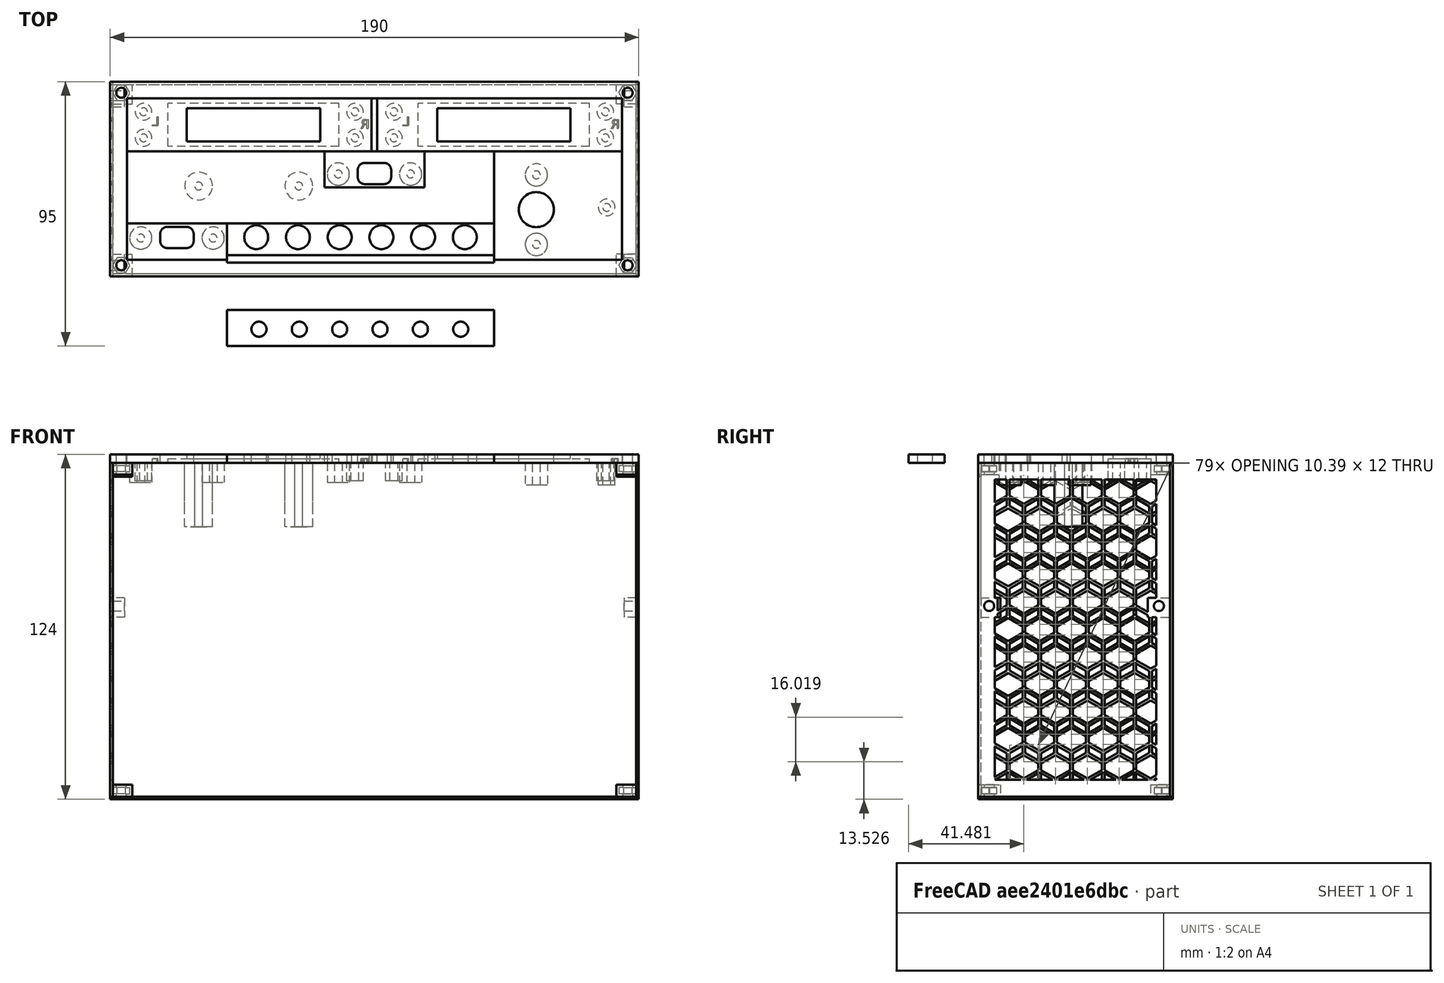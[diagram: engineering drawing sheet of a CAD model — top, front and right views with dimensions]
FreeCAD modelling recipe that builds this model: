
FCSTD DOCUMENT  (FreeCAD 0.18.4R)
Label: radio_led_grande
License: All rights reserved
LicenseURL: http://en.wikipedia.org/wiki/All_rights_reserved
objects: Part::Box×55, Part::Cut×51, Part::MultiFuse×42, Part::Cylinder×30, Part::Feature×20, Part::Prism×8, TechDraw::DrawSVGTemplate×1, TechDraw::DrawViewPart×1, TechDraw::DrawPage×1
note: 206 computed .brp shape members not serialized (recipe doc carries the construction recipe); baked Part::Feature solids carry a one-line shape summary decoded from their .brp

FEATURE [Part::Box] Box  label="Cube"
  AttacherType = Attacher::AttachEngine3D
  Height = 3
  Length = 190
  Width = 70
FEATURE [Part::Box] Box001  label="Cube001"
  AttacherType = Attacher::AttachEngine3D
  Height = 3
  Length = 178
  Placement = pos=(6,6,0) rot=(0,0,1;0rad)
  Width = 58
FEATURE [Part::Cut] Cut  label="marco"
  Base = -> Box
  Placement = pos=(-89,19,-107) rot=(0,0,1;0rad)
  Tool = -> Box001
FEATURE [Part::Box] Box002  label="Cube002"
  AttacherType = Attacher::AttachEngine3D
  Height = 3
  Length = 96
  Placement = pos=(-47,25,3) rot=(0,0,1;0rad)
  Width = 13
FEATURE [Part::Cylinder] Cylinder
  Angle = 360
  AttacherType = Attacher::AttachEngine3D
  Height = 10
  Placement = pos=(-35.5,31,0) rot=(0,0,1;0rad)
  Radius = 2.7
FEATURE [Part::Cylinder] Cylinder001 .. Cylinder005  x5 (patterned run collapsed; names and placements below)
  Angle = 360
  AttacherType = Attacher::AttachEngine3D
  Height = 10
  Radius = 2.7
  placements: 5 in arithmetic series — first pos=(-21,31,0) rot=(0,0,1;0rad), step (14.5,0,0), last pos=(37,31,0) rot=(0,0,1;0rad)
FEATURE [Part::Cut] Cut001001001002003001008002002033001001001001001001001002001001002001045002003017008007003
  Base = -> Box002
  Tool = -> Cylinder005
FEATURE [Part::Cut] Cut001001001002003001008002002033001001001001001001001002001001002001045002003017008007004
  Base = -> Cut001001001002003001008002002033001001001001001001001002001001002001045002003017008007003
  Tool = -> Cylinder004
FEATURE [Part::Cut] Cut001001001002003001008002002033001001001001001001001002001001002001045002003017008007005
  Base = -> Cut001001001002003001008002002033001001001001001001001002001001002001045002003017008007004
  Tool = -> Cylinder003
FEATURE [Part::Cut] Cut001001001002003001008002002033001001001001001001001002001001002001045002003017008007006
  Base = -> Cut001001001002003001008002002033001001001001001001001002001001002001045002003017008007005
  Tool = -> Cylinder002
FEATURE [Part::Cut] Cut001001001002003001008002002033001001001001001001001002001001002001045002003017008007007
  Base = -> Cut001001001002003001008002002033001001001001001001001002001001002001045002003017008007006
  Tool = -> Cylinder001
FEATURE [Part::Cut] Cut001001001002003001008002002033001001001001001001001002001001002001045002003017008007008  label="6leds_6mm_diametro"
  Base = -> Cut001001001002003001008002002033001001001001001001001002001001002001045002003017008007007
  Placement = pos=(0,-31,-110) rot=(0,0,1;0rad)
  Tool = -> Cylinder
FEATURE [Part::Box] Box003  label="Cube003"
  AttacherType = Attacher::AttachEngine3D
  Height = 3
  Length = 71
  Placement = pos=(-83,38,-107) rot=(0,0,1;0rad)
  Width = 26
FEATURE [Part::Box] Box004  label="Cube004"
  AttacherType = Attacher::AttachEngine3D
  Height = 3
  Length = 36
  Placement = pos=(-12,38,-107) rot=(0,0,1;0rad)
  Width = 13
FEATURE [Part::Box] Box005  label="Cube005"
  AttacherType = Attacher::AttachEngine3D
  Height = 3
  Length = 25
  Placement = pos=(24,38,-107) rot=(0,0,1;0rad)
  Width = 26
FEATURE [Part::Box] Box006  label="relleno2"
  AttacherType = Attacher::AttachEngine3D
  Height = 3
  Length = 2
  Placement = pos=(5,64,-107) rot=(0,0,1;0rad)
  Width = 19
FEATURE [Part::Box] Box007  label="Cube007"
  AttacherType = Attacher::AttachEngine3D
  Height = 3
  Length = 46
  Placement = pos=(49,61,-107) rot=(0,0,1;0rad)
  Width = 3
FEATURE [Part::Cylinder] Cylinder006
  Angle = 360
  AttacherType = Attacher::AttachEngine3D
  Height = 10
  Placement = pos=(-85,23,-111) rot=(0,0,1;0rad)
  Radius = 1.8
FEATURE [Part::Cylinder] Cylinder007
  Angle = 360
  AttacherType = Attacher::AttachEngine3D
  Height = 10
  Placement = pos=(-85,85,-113) rot=(0,0,1;0rad)
  Radius = 1.8
FEATURE [Part::Cylinder] Cylinder008
  Angle = 360
  AttacherType = Attacher::AttachEngine3D
  Height = 10
  Placement = pos=(97,23,-111) rot=(0,0,1;0rad)
  Radius = 1.8
FEATURE [Part::Cylinder] Cylinder009
  Angle = 360
  AttacherType = Attacher::AttachEngine3D
  Height = 10
  Placement = pos=(97,85,-111) rot=(0,0,1;0rad)
  Radius = 1.8
FEATURE [Part::Cut] Cut001001001002003001008002002033001001001001001001001002001001002001045002003017008007009
  Base = -> Cut
  Tool = -> Cylinder006
FEATURE [Part::Cut] Cut001001001002003001008002002033001001001001001001001002001001002001045002003017008007010
  Base = -> Cut001001001002003001008002002033001001001001001001001002001001002001045002003017008007009
  Tool = -> Cylinder007
FEATURE [Part::Cut] Cut001001001002003001008002002033001001001001001001001002001001002001045002003017008007011
  Base = -> Cut001001001002003001008002002033001001001001001001001002001001002001045002003017008007010
  Tool = -> Cylinder009
FEATURE [Part::Cut] Cut001001001002003001008002002033001001001001001001001002001001002001045002003017008007012  label="marco_con_agujeros"
  Base = -> Cut001001001002003001008002002033001001001001001001001002001001002001045002003017008007011
  Tool = -> Cylinder008
FEATURE [Part::Box] Box008  label="Cube008"
  AttacherType = Attacher::AttachEngine3D
  Height = 3
  Length = 96
  Placement = pos=(-47,24,-107) rot=(0,0,1;0rad)
  Width = 3
FEATURE [Part::MultiFuse] Fusion007002009027003005008003003014  label="soporte_alto_1"
  Placement = pos=(-164,36,0) rot=(0,0,1;0rad)
FEATURE [Part::MultiFuse] Fusion007002009027003005008003003006005002  label="soporte_alto_2"
  Placement = pos=(-128,36,0) rot=(0,0,1;0rad)
FEATURE [Part::Feature] Cut001001001002003001008002002033001001001001001001001002001001002001045002003017008007002010007002014003004001  label="base_boton_bajo_16x038_selector"
  Placement = pos=(-117,37,0) rot=(0,0,1;0rad)
  shape: bbox 36 x 16 x 10 mm, 26 faces (baked)
FEATURE [Part::Feature] Cut001001001002003001008002002033001001001001001001001002001001002001045002003017008007002010007002014003004002  label="base_boton_bajo_16x039_switch"
  Placement = pos=(-46,60,0) rot=(0,0,1;0rad)
  shape: bbox 36 x 16 x 10 mm, 26 faces (baked)
FEATURE [Part::Feature] Cut001001001002003001008002002033001001001001001001001002001001002001045002003017008007002010007002014003013001  label="base_7seg_full_3mm_88x021_stby"
  Placement = pos=(2,0,0) rot=(0,0,1;0rad)
  shape: bbox 88 x 19 x 9.5 mm, 63 faces (baked)
FEATURE [Part::Feature] Cut001001001002003001008002002033001001001001001001001002001001002001045002003017008007002010007002014003013002  label="base_7seg_full_3mm_88x022_act"
  Placement = pos=(-88,0,0) rot=(0,0,1;0rad)
  shape: bbox 88 x 19 x 9.5 mm, 63 faces (baked)
FEATURE [Part::Feature] Fusion007002009027003005008003003018001  label="base_encoder_doble_46x36_agujero_13"
  Placement = pos=(102.5,-18,0) rot=(0,0,1;0rad)
  shape: bbox 46 x 36 x 11 mm, 19 faces (baked)
FEATURE [Part::Feature] Cut001001001002003001008002002033001001001001001001001002001001002001045002003017008007002010007002014003017001  label="base_led_radius_43_ref"
  Placement = pos=(-26,-22,0) rot=(0,0,1;0rad)
  shape: bbox 10.6 x 10.6 x 3 mm, 7 faces (baked)
FEATURE [Part::Feature] Cut001001001002003001008002002033001001001001001001001002001001002001045002003017008007002010007002014003017002  label="base_led_radius_43_ref001"
  Placement = pos=(-11,-22,0) rot=(0,0,1;0rad)
  shape: bbox 10.6 x 10.6 x 3 mm, 7 faces (baked)
FEATURE [Part::Feature] Cut001001001002003001008002002033001001001001001001001002001001002001045002003017008007002010007002014003017003  label="base_led_radius_43_ref002"
  Placement = pos=(4,-22,0) rot=(0,0,1;0rad)
  shape: bbox 10.6 x 10.6 x 3 mm, 7 faces (baked)
FEATURE [Part::Feature] Cut001001001002003001008002002033001001001001001001001002001001002001045002003017008007002010007002014003017004  label="base_led_radius_43_ref003"
  Placement = pos=(19,-22,0) rot=(0,0,1;0rad)
  shape: bbox 10.6 x 10.6 x 3 mm, 7 faces (baked)
FEATURE [Part::Feature] Cut001001001002003001008002002033001001001001001001001002001001002001045002003017008007002010007002014003017005  label="base_led_radius_43_ref004"
  Placement = pos=(34,-22,0) rot=(0,0,1;0rad)
  shape: bbox 10.6 x 10.6 x 3 mm, 7 faces (baked)
FEATURE [Part::Feature] Cut001001001002003001008002002033001001001001001001001002001001002001045002003017008007002010007002014003017006  label="base_led_radius_43_ref005"
  Placement = pos=(49,-22,0) rot=(0,0,1;0rad)
  shape: bbox 10.6 x 10.6 x 3 mm, 7 faces (baked)
FEATURE [Part::Box] Box009  label="Cube009"
  AttacherType = Attacher::AttachEngine3D
  Height = 3
  Length = 96
  Placement = pos=(-31.2,-6.2,-108) rot=(0,0,1;0rad)
  Width = 13
FEATURE [Part::Box] Box010  label="Cube010"
  AttacherType = Attacher::AttachEngine3D
  Height = 3
  Length = 85
  Placement = pos=(-25.5,-4.7,-108) rot=(0,0,1;0rad)
  Width = 10
FEATURE [Part::Cut] Cut001001001002003001008002002033001001001001001001001002001001002001045002003017008007002010007002014003017007
  Base = -> Box009
  Tool = -> Box010
FEATURE [Part::Box] Box011  label="Cube011"
  AttacherType = Attacher::AttachEngine3D
  Height = 3
  Length = 6
  Placement = pos=(-16.2,-6,-108) rot=(0,0,1;0rad)
  Width = 12
FEATURE [Part::Box] Box012  label="Cube012"
  AttacherType = Attacher::AttachEngine3D
  Height = 3
  Length = 6
  Placement = pos=(-1.2,-6,-108) rot=(0,0,1;0rad)
  Width = 12
FEATURE [Part::Box] Box013  label="Cube013"
  AttacherType = Attacher::AttachEngine3D
  Height = 3
  Length = 6
  Placement = pos=(13.8,-6,-108) rot=(0,0,1;0rad)
  Width = 12
FEATURE [Part::Box] Box014  label="Cube014"
  AttacherType = Attacher::AttachEngine3D
  Height = 3
  Length = 6
  Placement = pos=(28.8,-6,-108) rot=(0,0,1;0rad)
  Width = 12
FEATURE [Part::Box] Box015  label="Cube015"
  AttacherType = Attacher::AttachEngine3D
  Height = 3
  Length = 6
  Placement = pos=(43.8,-6,-108) rot=(0,0,1;0rad)
  Width = 12
FEATURE [Part::MultiFuse] Fusion007002009027003005008003003006005005
  Shapes = -> [Cut001001001002003001008002002033001001001001001001001002001001002001045002003017008007002010007002014003017007,Box011]
FEATURE [Part::MultiFuse] Fusion007002009027003005008003003006005006
  Shapes = -> [Fusion007002009027003005008003003006005005,Box015]
FEATURE [Part::MultiFuse] Fusion007002009027003005008003003006005007
  Shapes = -> [Fusion007002009027003005008003003006005006,Box014]
FEATURE [Part::MultiFuse] Fusion007002009027003005008003003006005008
  Shapes = -> [Fusion007002009027003005008003003006005007,Box013]
FEATURE [Part::MultiFuse] Fusion007002009027003005008003003006005009
  Placement = pos=(0,0,1) rot=(0,0,1;0rad)
  Shapes = -> [Fusion007002009027003005008003003006005008,Box012]
FEATURE [Part::MultiFuse] Fusion007002009027003005008003003006005010
  Shapes = -> [Fusion007002009027003005008003003006005009,Cut001001001002003001008002002033001001001001001001001002001001002001045002003017008007002010007002014003017006]
FEATURE [Part::MultiFuse] Fusion007002009027003005008003003006005011
  Shapes = -> [Fusion007002009027003005008003003006005010,Cut001001001002003001008002002033001001001001001001001002001001002001045002003017008007002010007002014003017005]
FEATURE [Part::MultiFuse] Fusion007002009027003005008003003006005012
  Shapes = -> [Fusion007002009027003005008003003006005011,Cut001001001002003001008002002033001001001001001001001002001001002001045002003017008007002010007002014003017004]
FEATURE [Part::MultiFuse] Fusion007002009027003005008003003006005013
  Shapes = -> [Fusion007002009027003005008003003006005012,Cut001001001002003001008002002033001001001001001001001002001001002001045002003017008007002010007002014003017003]
FEATURE [Part::MultiFuse] Fusion007002009027003005008003003006005014
  Shapes = -> [Fusion007002009027003005008003003006005013,Cut001001001002003001008002002033001001001001001001001002001001002001045002003017008007002010007002014003017002]
FEATURE [Part::MultiFuse] Fusion007002009027003005008003003006005015  label="6_leds_grandes"
  Placement = pos=(-15.8,32.8,0) rot=(0,0,1;0rad)
  Shapes = -> [Fusion007002009027003005008003003006005014,Cut001001001002003001008002002033001001001001001001001002001001002001045002003017008007002010007002014003017001]
FEATURE [Part::MultiFuse] Fusion
  Shapes = -> [Box003,Box004,Box005]
FEATURE [Part::Feature] Fusion007002009027003005008003003006005016  label="Fusion007002009027003005008003003006005015"
  shape: bbox 132 x 26 x 3 mm, 10 faces (baked)
FEATURE [Part::MultiFuse] Fusion007002009027003005008003003006005017
  Shapes = -> [Fusion007002009027003005008003003006005016,Cut001001001002003001008002002033001001001001001001001002001001002001045002003017008007002010007002014003004002]
FEATURE [Part::Feature] Fusion007002009027003005008003003006005017001  label="Fusion007002009027003005008003003006005018"
  shape: bbox 132 x 26 x 10 mm, 22 faces (baked)
FEATURE [Part::MultiFuse] Fusion007002009027003005008003003006005017002
  Shapes = -> [Fusion007002009027003005008003003006005017001,Cut001001001002003001008002002033001001001001001001001002001001002001045002003017008007002010007002014003004001]
FEATURE [Part::Feature] Fusion007002009027003005008003003006005017002001  label="Fusion007002009027003005008003003006005017003"
  shape: bbox 132 x 39 x 10 mm, 40 faces (baked)
FEATURE [Part::MultiFuse] Fusion007002009027003005008003003006005017002002
  Shapes = -> [Fusion007002009027003005008003003006005017002001,Fusion007002009027003005008003003018001,Box007]
FEATURE [Part::Feature] Fusion007002009027003005008003003006005017002002001  label="Fusion007002009027003005008003003006005017002003"
  shape: bbox 178 x 39 x 11 mm, 55 faces (baked)
FEATURE [Part::MultiFuse] Fusion007002009027003005008003003006005017002002002
  Shapes = -> [Fusion007002009027003005008003003006005017002002001,Fusion007002009027003005008003003006005015]
FEATURE [Part::Feature] Fusion007002009027003005008003003006005017002002002001  label="Fusion007002009027003005008003003006005017002002003"
  shape: bbox 178 x 39 x 11 mm, 61 faces (baked)
FEATURE [Part::MultiFuse] Fusion007002009027003005008003003006005017002002002002
  Shapes = -> [Fusion007002009027003005008003003006005017002002002001,Box008,Box006]
FEATURE [Part::Feature] Fusion007002009027003005008003003006005017002002002002001  label="Fusion007002009027003005008003003006005017002002002003"
  shape: bbox 178 x 59 x 11 mm, 65 faces (baked)
FEATURE [Part::MultiFuse] Fusion007002009027003005008003003006005017002002002002002
  Shapes = -> [Fusion007002009027003005008003003006005017002002002002001,Cut001001001002003001008002002033001001001001001001001002001001002001045002003017008007002010007002014003013002,Cut001001001002003001008002002033001001001001001001001002001001002001045002003017008007002010007002014003013001]
FEATURE [Part::Feature] Fusion007002009027003005008003003006005017002002002002002001  label="Fusion007002009027003005008003003006005017002002002002003"
  shape: bbox 178 x 59 x 11 mm, 175 faces (baked)
FEATURE [Part::MultiFuse] Fusion007002009027003005008003003006005017002002002002002002
  Shapes = -> [Fusion007002009027003005008003003006005017002002002002002001,Cut001001001002003001008002002033001001001001001001001002001001002001045002003017008007012]
FEATURE [Part::Feature] Fusion007002009027003005008003003006005017002002002002002002001  label="Fusion007002009027003005008003003006005017002002002002002003"
  shape: bbox 190 x 70 x 11 mm, 175 faces (baked)
FEATURE [Part::MultiFuse] Fusion007002009027003005008003003006005017002002002002002002002
  Shapes = -> [Fusion007002009027003005008003003006005017002002002002002002001,Fusion007002009027003005008003003014,Fusion007002009027003005008003003006005002]
FEATURE [Part::Feature] Fusion007002009027003005008003003006005017002002002002002002002001  label="radio_con_leds_grandes"
  shape: bbox 190 x 70 x 26 mm, 183 faces (baked)
FEATURE [TechDraw::DrawSVGTemplate] Template
  Height = 210
  Orientation = 1
  Width = 297
FEATURE [TechDraw::DrawViewPart] View
  CoarseView = true
  Direction = (0,0,-1)
  Focus = 100
  HardHidden = false
  IsoCount = 0
  IsoHidden = false
  IsoVisible = false
  LockPosition = false
  Perspective = false
  Rotation = 0
  ScaleType = 2
  SeamHidden = false
  SeamVisible = false
  SmoothHidden = false
  SmoothVisible = false
  Source = -> [Fusion007002009027003005008003003006005017002002002002002002002001]
  X = 148.5
  Y = 105
FEATURE [TechDraw::DrawPage] Page
  KeepUpdated = true
  ProjectionType = 0
  Template = -> Template
  Views = -> [View]
FEATURE [Part::Box] Box016  label="base"
  AttacherType = Attacher::AttachEngine3D
  Height = 120
  Length = 188
  Placement = pos=(-88,19,-227) rot=(0,0,1;0rad)
  Width = 1
FEATURE [Part::Box] Box017  label="izquierda"
  AttacherType = Attacher::AttachEngine3D
  Height = 120
  Length = 1
  Placement = pos=(-89,19,-227) rot=(0,0,1;0rad)
  Width = 70
FEATURE [Part::Box] Box019  label="tapa"
  AttacherType = Attacher::AttachEngine3D
  Height = 120
  Length = 188
  Placement = pos=(-88,88,-227) rot=(0,0,1;0rad)
  Width = 1
FEATURE [Part::Box] Box020  label="Cube016"
  AttacherType = Attacher::AttachEngine3D
  Height = 4.2
  Length = 7
  Placement = pos=(-88,19,-111.2) rot=(0,0,1;0rad)
  Width = 8
FEATURE [Part::Cylinder] Cylinder010
  Angle = 360
  AttacherType = Attacher::AttachEngine3D
  Height = 10
  Placement = pos=(-85,23,-112) rot=(0,0,1;0rad)
  Radius = 1.8
FEATURE [Part::Cut] Cut001001001002003001008002002033001001001001001001001002001001002001045002003017008007002010007002014003017008
  Base = -> Box020
  Tool = -> Cylinder010
FEATURE [Part::Prism] Prism001
  AttacherType = Attacher::AttachEngine3D
  Circumradius = 3.1
  Height = 2.2
  Placement = pos=(-85,23,-110.2) rot=(0,0,1;0rad)
  Polygon = 6
FEATURE [Part::Cut] Cut001001001002003001008002002033001001001001001001001002001001002001045002003017008007002010007002014003017009
  Base = -> Cut001001001002003001008002002033001001001001001001001002001001002001045002003017008007002010007002014003017008
  Tool = -> Prism001
FEATURE [Part::Box] Box021  label="Cube017"
  AttacherType = Attacher::AttachEngine3D
  Height = 4.2
  Length = 7
  Placement = pos=(-88,81,-111.2) rot=(0,0,1;0rad)
  Width = 8
FEATURE [Part::Cylinder] Cylinder011
  Angle = 360
  AttacherType = Attacher::AttachEngine3D
  Height = 10
  Placement = pos=(-85,85,-112) rot=(0,0,1;0rad)
  Radius = 1.8
FEATURE [Part::Prism] Prism002
  AttacherType = Attacher::AttachEngine3D
  Circumradius = 3.1
  Height = 2.2
  Placement = pos=(-85,85,-110.2) rot=(0,0,1;0rad)
  Polygon = 6
FEATURE [Part::Cut] Cut001001001002003001008002002033001001001001001001001002001001002001045002003017008007002010007002014003017010
  Base = -> Box021
  Tool = -> Cylinder011
FEATURE [Part::Cut] Cut001001001002003001008002002033001001001001001001001002001001002001045002003017008007002010007002014003017011
  Base = -> Cut001001001002003001008002002033001001001001001001001002001001002001045002003017008007002010007002014003017010
  Tool = -> Prism002
FEATURE [Part::MultiFuse] Fusion007002009027003005008003003006005017002002002002002002002002
  Shapes = -> [Box017,Cut001001001002003001008002002033001001001001001001001002001001002001045002003017008007002010007002014003017009]
FEATURE [Part::MultiFuse] Fusion007002009027003005008003003006005017002002002002002002002003
  Shapes = -> [Fusion007002009027003005008003003006005017002002002002002002002002,Cut001001001002003001008002002033001001001001001001001002001001002001045002003017008007002010007002014003017011]
FEATURE [Part::Cylinder] Cylinder012
  Angle = 360
  AttacherType = Attacher::AttachEngine3D
  Height = 10
  Placement = pos=(-85,85,-112) rot=(0,0,1;0rad)
  Radius = 1.8
FEATURE [Part::Box] Box022  label="Cube018"
  AttacherType = Attacher::AttachEngine3D
  Height = 4.2
  Length = 7
  Placement = pos=(-88,81,-111.2) rot=(0,0,1;0rad)
  Width = 8
FEATURE [Part::Cut] Cut001001001002003001008002002033001001001001001001001002001001002001045002003017008007002010007002014003017012
  Base = -> Box022
  Tool = -> Cylinder012
FEATURE [Part::Prism] Prism003
  AttacherType = Attacher::AttachEngine3D
  Circumradius = 3.1
  Height = 2.2
  Placement = pos=(-85,85,-110.2) rot=(0,0,1;0rad)
  Polygon = 6
FEATURE [Part::Cut] Cut001001001002003001008002002033001001001001001001001002001001002001045002003017008007002010007002014003017013
  Base = -> Cut001001001002003001008002002033001001001001001001001002001001002001045002003017008007002010007002014003017012
  Placement = pos=(0,0,-115.8) rot=(0,0,1;0rad)
  Tool = -> Prism003
FEATURE [Part::Cylinder] Cylinder013
  Angle = 360
  AttacherType = Attacher::AttachEngine3D
  Height = 10
  Placement = pos=(-85,23,-112) rot=(0,0,1;0rad)
  Radius = 1.8
FEATURE [Part::Box] Box023  label="Cube019"
  AttacherType = Attacher::AttachEngine3D
  Height = 4.2
  Length = 7
  Placement = pos=(-88,19,-111.2) rot=(0,0,1;0rad)
  Width = 8
FEATURE [Part::Prism] Prism004
  AttacherType = Attacher::AttachEngine3D
  Circumradius = 3.1
  Height = 2.2
  Placement = pos=(-85,23,-110.2) rot=(0,0,1;0rad)
  Polygon = 6
FEATURE [Part::Cut] Cut001001001002003001008002002033001001001001001001001002001001002001045002003017008007002010007002014003017014
  Base = -> Box023
  Tool = -> Cylinder013
FEATURE [Part::Cut] Cut001001001002003001008002002033001001001001001001001002001001002001045002003017008007002010007002014003017015
  Base = -> Cut001001001002003001008002002033001001001001001001001002001001002001045002003017008007002010007002014003017014
  Placement = pos=(0,0,-115.8) rot=(0,0,1;0rad)
  Tool = -> Prism004
FEATURE [Part::MultiFuse] Fusion007002009027003005008003003006005017002002002002002002002004
  Shapes = -> [Fusion007002009027003005008003003006005017002002002002002002002003,Cut001001001002003001008002002033001001001001001001001002001001002001045002003017008007002010007002014003017013]
FEATURE [Part::MultiFuse] Fusion007002009027003005008003003006005017002002002002002002002005  label="lateral_izquierdo"
  Shapes = -> [Fusion007002009027003005008003003006005017002002002002002002002004,Cut001001001002003001008002002033001001001001001001001002001001002001045002003017008007002010007002014003017015]
FEATURE [Part::Box] Box029  label="izquierda002"
  AttacherType = Attacher::AttachEngine3D
  Height = 120
  Length = 1
  Placement = pos=(-89,19,-227) rot=(0,0,1;0rad)
  Width = 70
FEATURE [Part::Box] Box030  label="placa1"
  AttacherType = Attacher::AttachEngine3D
  Height = 120
  Length = 1
  Placement = pos=(-89,19,-227) rot=(0,0,1;0rad)
  Width = 70
FEATURE [Part::Box] Box031  label="placa002"
  AttacherType = Attacher::AttachEngine3D
  Height = 108
  Length = 1
  Placement = pos=(-89,25,-221) rot=(0,0,1;0rad)
  Width = 58
FEATURE [Part::Box] Box032  label="placa003"
  AttacherType = Attacher::AttachEngine3D
  Height = 120
  Length = 1
  Placement = pos=(-89,19,-227) rot=(0,0,1;0rad)
  Width = 70
FEATURE [Part::Cut] Cut001001001002003001008002002033001001001001001001001002001001002001045002003017008007002010007002014003017024
  Base = -> Box030
  Tool = -> Box031
FEATURE [Part::Box] Box033  label="corta_medio"
  AttacherType = Attacher::AttachEngine3D
  Height = 108
  Length = 1
  Placement = pos=(-89,25,-221) rot=(0,0,1;0rad)
  Width = 58
FEATURE [Part::MultiFuse] Fusion007002009027003005008003003006005017002002002002002002002010
  Shapes = -> [Cut001001001002003001008002002033001001001001001001001002001001002001045002003017008007002010007002014003017024,Cut]
FEATURE [Part::Cut] Cut001001001002003001008002002033001001001001001001001002001001002001045002003017008007002010007002014003017025
  Base = -> Fusion007002009027003005008003003006005017002002002002002002002005
  Tool = -> Box033
FEATURE [Part::MultiFuse] Fusion007002009027003005008003003006005017002002002002002002002011  label="placa_lateral_izquierda_panal_alto"
  Shapes = -> [Fusion007002009027003005008003003006005017002002002002002002002010,Cut001001001002003001008002002033001001001001001001001002001001002001045002003017008007002010007002014003017025]
FEATURE [Part::Box] Box034  label="Cube020"
  AttacherType = Attacher::AttachEngine3D
  Height = 150
  Length = 10
  Placement = pos=(-90,88,-257) rot=(0,0,1;0rad)
  Width = 10
FEATURE [Part::Cut] Cut001001001002003001008002002033001001001001001001001002001001002001045002003017008007002010007002014003017026  label="placa_lateral_izquierda_panal"
  Base = -> Fusion007002009027003005008003003006005017002002002002002002002011
  Tool = -> Box034
FEATURE [Part::Box] Box035  label="placa004"
  AttacherType = Attacher::AttachEngine3D
  Height = 108
  Length = 1
  Placement = pos=(-89,25,-221) rot=(0,0,1;0rad)
  Width = 58
FEATURE [Part::Box] Box036  label="Cube021"
  AttacherType = Attacher::AttachEngine3D
  Height = 4.2
  Length = 7
  Placement = pos=(-88,81,-111.2) rot=(0,0,1;0rad)
  Width = 8
FEATURE [Part::Prism] Prism005
  AttacherType = Attacher::AttachEngine3D
  Circumradius = 3.1
  Height = 2.2
  Placement = pos=(-85,85,-110.2) rot=(0,0,1;0rad)
  Polygon = 6
FEATURE [Part::Prism] Prism006
  AttacherType = Attacher::AttachEngine3D
  Circumradius = 3.1
  Height = 2.2
  Placement = pos=(-85,85,-110.2) rot=(0,0,1;0rad)
  Polygon = 6
FEATURE [Part::Box] Box037  label="izquierda003"
  AttacherType = Attacher::AttachEngine3D
  Height = 120
  Length = 1
  Placement = pos=(-89,19,-227) rot=(0,0,1;0rad)
  Width = 70
FEATURE [Part::Box] Box038  label="placa005"
  AttacherType = Attacher::AttachEngine3D
  Height = 120
  Length = 1
  Placement = pos=(-89,19,-227) rot=(0,0,1;0rad)
  Width = 70
FEATURE [Part::Prism] Prism007
  AttacherType = Attacher::AttachEngine3D
  Circumradius = 3.1
  Height = 2.2
  Placement = pos=(-85,23,-110.2) rot=(0,0,1;0rad)
  Polygon = 6
FEATURE [Part::Cut] Cut001001001002003001008002002033001001001001001001001002001001002001045002003017008007002010007002014003017030
  Base = -> Box038
  Tool = -> Box035
FEATURE [Part::Box] Box039  label="Cube022"
  AttacherType = Attacher::AttachEngine3D
  Height = 4.2
  Length = 7
  Placement = pos=(-88,19,-111.2) rot=(0,0,1;0rad)
  Width = 8
FEATURE [Part::Box] Box040  label="corta_medio001"
  AttacherType = Attacher::AttachEngine3D
  Height = 108
  Length = 1
  Placement = pos=(-89,25,-221) rot=(0,0,1;0rad)
  Width = 58
FEATURE [Part::Box] Box041  label="Cube023"
  AttacherType = Attacher::AttachEngine3D
  Height = 150
  Length = 10
  Placement = pos=(-90,88,-257) rot=(0,0,1;0rad)
  Width = 10
FEATURE [Part::Box] Box042  label="Cube024"
  AttacherType = Attacher::AttachEngine3D
  Height = 4.2
  Length = 7
  Placement = pos=(-88,19,-111.2) rot=(0,0,1;0rad)
  Width = 8
FEATURE [Part::Box] Box043  label="Cube025"
  AttacherType = Attacher::AttachEngine3D
  Height = 4.2
  Length = 7
  Placement = pos=(-88,81,-111.2) rot=(0,0,1;0rad)
  Width = 8
FEATURE [Part::Box] Box044  label="Cube026"
  AttacherType = Attacher::AttachEngine3D
  Height = 3
  Length = 178
  Placement = pos=(6,6,0) rot=(0,0,1;0rad)
  Width = 58
FEATURE [Part::Prism] Prism008
  AttacherType = Attacher::AttachEngine3D
  Circumradius = 3.1
  Height = 2.2
  Placement = pos=(-85,23,-110.2) rot=(0,0,1;0rad)
  Polygon = 6
FEATURE [Part::Cylinder] Cylinder014
  Angle = 360
  AttacherType = Attacher::AttachEngine3D
  Height = 10
  Placement = pos=(-85,23,-112) rot=(0,0,1;0rad)
  Radius = 1.8
FEATURE [Part::Cut] Cut001001001002003001008002002033001001001001001001001002001001002001045002003017008007002010007002014003017029
  Base = -> Box042
  Tool = -> Cylinder014
FEATURE [Part::Cylinder] Cylinder015
  Angle = 360
  AttacherType = Attacher::AttachEngine3D
  Height = 10
  Placement = pos=(-85,85,-112) rot=(0,0,1;0rad)
  Radius = 1.8
FEATURE [Part::Cylinder] Cylinder016
  Angle = 360
  AttacherType = Attacher::AttachEngine3D
  Height = 10
  Placement = pos=(-85,23,-112) rot=(0,0,1;0rad)
  Radius = 1.8
FEATURE [Part::Cylinder] Cylinder017
  Angle = 360
  AttacherType = Attacher::AttachEngine3D
  Height = 10
  Placement = pos=(-85,85,-112) rot=(0,0,1;0rad)
  Radius = 1.8
FEATURE [Part::Cut] Cut001001001002003001008002002033001001001001001001001002001001002001045002003017008007002010007002014003017034
  Base = -> Box043
  Tool = -> Cylinder015
FEATURE [Part::Cut] Cut001001001002003001008002002033001001001001001001001002001001002001045002003017008007002010007002014003017033
  Base = -> Cut001001001002003001008002002033001001001001001001001002001001002001045002003017008007002010007002014003017034
  Placement = pos=(0,0,-115.8) rot=(0,0,1;0rad)
  Tool = -> Prism005
FEATURE [Part::Cut] Cut001001001002003001008002002033001001001001001001001002001001002001045002003017008007002010007002014003017035
  Base = -> Box036
  Tool = -> Cylinder017
FEATURE [Part::Cut] Cut001001001002003001008002002033001001001001001001001002001001002001045002003017008007002010007002014003017031
  Base = -> Cut001001001002003001008002002033001001001001001001001002001001002001045002003017008007002010007002014003017035
  Tool = -> Prism006
FEATURE [Part::Cut] Cut001001001002003001008002002033001001001001001001001002001001002001045002003017008007002010007002014003017036
  Base = -> Cut001001001002003001008002002033001001001001001001001002001001002001045002003017008007002010007002014003017029
  Placement = pos=(0,0,-115.8) rot=(0,0,1;0rad)
  Tool = -> Prism008
FEATURE [Part::Box] Box045  label="Cube027"
  AttacherType = Attacher::AttachEngine3D
  Height = 3
  Length = 190
  Width = 70
FEATURE [Part::Cut] Cut001001001002003001008002002033001001001001001001001002001001002001045002003017008007002010007002014003017027  label="marco001"
  Base = -> Box045
  Placement = pos=(-89,19,-107) rot=(0,0,1;0rad)
  Tool = -> Box044
FEATURE [Part::MultiFuse] Fusion007002009027003005008003003006005017002002002002002002002014
  Shapes = -> [Cut001001001002003001008002002033001001001001001001001002001001002001045002003017008007002010007002014003017030,Cut001001001002003001008002002033001001001001001001001002001001002001045002003017008007002010007002014003017027]
FEATURE [Part::Cut] Cut001001001002003001008002002033001001001001001001001002001001002001045002003017008007002010007002014003017038
  Base = -> Box039
  Tool = -> Cylinder016
FEATURE [Part::Cut] Cut001001001002003001008002002033001001001001001001001002001001002001045002003017008007002010007002014003017037
  Base = -> Cut001001001002003001008002002033001001001001001001001002001001002001045002003017008007002010007002014003017038
  Tool = -> Prism007
FEATURE [Part::MultiFuse] Fusion007002009027003005008003003006005017002002002002002002002013
  Shapes = -> [Box037,Cut001001001002003001008002002033001001001001001001001002001001002001045002003017008007002010007002014003017037]
FEATURE [Part::MultiFuse] Fusion007002009027003005008003003006005017002002002002002002002015
  Shapes = -> [Fusion007002009027003005008003003006005017002002002002002002002013,Cut001001001002003001008002002033001001001001001001001002001001002001045002003017008007002010007002014003017031]
FEATURE [Part::MultiFuse] Fusion007002009027003005008003003006005017002002002002002002002012
  Shapes = -> [Fusion007002009027003005008003003006005017002002002002002002002015,Cut001001001002003001008002002033001001001001001001001002001001002001045002003017008007002010007002014003017033]
FEATURE [Part::MultiFuse] Fusion007002009027003005008003003006005017002002002002002002002016  label="lateral_izquierdo001"
  Shapes = -> [Fusion007002009027003005008003003006005017002002002002002002002012,Cut001001001002003001008002002033001001001001001001001002001001002001045002003017008007002010007002014003017036]
FEATURE [Part::Cut] Cut001001001002003001008002002033001001001001001001001002001001002001045002003017008007002010007002014003017028
  Base = -> Fusion007002009027003005008003003006005017002002002002002002002016
  Tool = -> Box040
FEATURE [Part::MultiFuse] Fusion007002009027003005008003003006005017002002002002002002002017  label="placa_lateral_izquierda_panal_alto001"
  Shapes = -> [Fusion007002009027003005008003003006005017002002002002002002002014,Cut001001001002003001008002002033001001001001001001001002001001002001045002003017008007002010007002014003017028]
FEATURE [Part::Cut] Cut001001001002003001008002002033001001001001001001001002001001002001045002003017008007002010007002014003017032  label="placa_lateral_derecha_panal"
  Base = -> Fusion007002009027003005008003003006005017002002002002002002002017
  Placement = pos=(12,0,-334) rot=(0,1,0;3.14159rad)
  Tool = -> Box041
FEATURE [Part::Box] Box046  label="Cube028"
  AttacherType = Attacher::AttachEngine3D
  Height = 120
  Length = 190
  Placement = pos=(-89,88,-227) rot=(0,0,1;0rad)
  Width = 1
FEATURE [Part::Box] Box047  label="Cube029"
  AttacherType = Attacher::AttachEngine3D
  Height = 4.2
  Length = 7
  Placement = pos=(-88,19,-111.2) rot=(0,0,1;0rad)
  Width = 8
FEATURE [Part::Cylinder] Cylinder018
  Angle = 360
  AttacherType = Attacher::AttachEngine3D
  Height = 10
  Placement = pos=(-85,23,-112) rot=(0,0,1;0rad)
  Radius = 1.8
FEATURE [Part::Cut] Cut001001001002003001008002002033001001001001001001001002001001002001045002003017008007002010007002014003017039
  Base = -> Box047
  Placement = pos=(23.2,61,-243.5) rot=(0,1,0;1.5708rad)
  Tool = -> Cylinder018
FEATURE [Part::Cylinder] Cylinder019
  Angle = 360
  AttacherType = Attacher::AttachEngine3D
  Height = 10
  Placement = pos=(-85,23,-112) rot=(0,0,1;0rad)
  Radius = 1.8
FEATURE [Part::Box] Box048  label="Cube030"
  AttacherType = Attacher::AttachEngine3D
  Height = 4.2
  Length = 7
  Placement = pos=(-88,19,-111.2) rot=(0,0,1;0rad)
  Width = 8
FEATURE [Part::Cut] Cut001001001002003001008002002033001001001001001001001002001001002001045002003017008007002010007002014003017040
  Base = -> Box048
  Placement = pos=(207,61,-243.5) rot=(0,1,0;1.5708rad)
  Tool = -> Cylinder019
FEATURE [Part::MultiFuse] Fusion007002009027003005008003003006005017002002002002002002002018
  Shapes = -> [Box046,Cut001001001002003001008002002033001001001001001001001002001001002001045002003017008007002010007002014003017039]
FEATURE [Part::MultiFuse] Fusion007002009027003005008003003006005017002002002002002002002019  label="placa_tapa_sin_panal"
  Shapes = -> [Fusion007002009027003005008003003006005017002002002002002002002018,Cut001001001002003001008002002033001001001001001001001002001001002001045002003017008007002010007002014003017040]
FEATURE [Part::Box] Box049  label="pestania"
  AttacherType = Attacher::AttachEngine3D
  Height = 7
  Length = 1
  Placement = pos=(100,80,-162.5) rot=(0,0,1;0rad)
  Width = 7
FEATURE [Part::Box] Box050  label="pestania001"
  AttacherType = Attacher::AttachEngine3D
  Height = 7
  Length = 1
  Placement = pos=(-89,80,-162.5) rot=(0,0,1;0rad)
  Width = 7
FEATURE [Part::MultiFuse] Fusion007002009027003005008003003006005017002002002002002002002020  label="placa_lateral_derecha_panal_sin_agujero"
  Shapes = -> [Box049,Cut001001001002003001008002002033001001001001001001001002001001002001045002003017008007002010007002014003017032]
FEATURE [Part::MultiFuse] Fusion007002009027003005008003003006005017002002002002002002002021  label="placa_lateral_izquierda_panal_sin_agujero"
  Shapes = -> [Cut001001001002003001008002002033001001001001001001001002001001002001045002003017008007002010007002014003017026,Box050]
FEATURE [Part::Cylinder] Cylinder020
  Angle = 360
  AttacherType = Attacher::AttachEngine3D
  Height = 210
  Placement = pos=(-100,84,-158.5) rot=(0,1,0;1.5708rad)
  Radius = 1.8
FEATURE [Part::Cylinder] Cylinder021
  Angle = 360
  AttacherType = Attacher::AttachEngine3D
  Height = 210
  Placement = pos=(-100,84,-158.5) rot=(0,1,0;1.5708rad)
  Radius = 1.8
FEATURE [Part::Cut] Cut001001001002003001008002002033001001001001001001001002001001002001045002003017008007002010007002014003017041  label="placa_lateral_derecha_panal_1"
  Base = -> Fusion007002009027003005008003003006005017002002002002002002002020
  Tool = -> Cylinder020
FEATURE [Part::Cut] Cut001001001002003001008002002033001001001001001001001002001001002001045002003017008007002010007002014003017042  label="placa_lateral_izquierda_panal_1"
  Base = -> Fusion007002009027003005008003003006005017002002002002002002002021
  Tool = -> Cylinder021
FEATURE [Part::Cylinder] Cylinder022
  Angle = 360
  AttacherType = Attacher::AttachEngine3D
  Height = 10
  Placement = pos=(-85,23,-112) rot=(0,0,1;0rad)
  Radius = 1.8
FEATURE [Part::Box] Box051  label="Cube031"
  AttacherType = Attacher::AttachEngine3D
  Height = 4.2
  Length = 7
  Placement = pos=(-88,19,-111.2) rot=(0,0,1;0rad)
  Width = 8
FEATURE [Part::Cut] Cut001001001002003001008002002033001001001001001001001002001001002001045002003017008007002010007002014003017043  label="porta_tornillo_1"
  Base = -> Box051
  Placement = pos=(23.2,0,-243.5) rot=(0,1,0;1.5708rad)
  Tool = -> Cylinder022
FEATURE [Part::Cylinder] Cylinder023
  Angle = 360
  AttacherType = Attacher::AttachEngine3D
  Height = 10
  Placement = pos=(-85,23,-112) rot=(0,0,1;0rad)
  Radius = 1.8
FEATURE [Part::Box] Box052  label="Cube032"
  AttacherType = Attacher::AttachEngine3D
  Height = 4.2
  Length = 7
  Placement = pos=(-88,19,-111.2) rot=(0,0,1;0rad)
  Width = 8
FEATURE [Part::Cut] Cut001001001002003001008002002033001001001001001001001002001001002001045002003017008007002010007002014003017044  label="porta_tornillo_2"
  Base = -> Box052
  Placement = pos=(207,0,-243.5) rot=(0,1,0;1.5708rad)
  Tool = -> Cylinder023
FEATURE [Part::Cylinder] Cylinder024
  Angle = 360
  AttacherType = Attacher::AttachEngine3D
  Height = 210
  Placement = pos=(-100,23,-158.5) rot=(0,1,0;1.5708rad)
  Radius = 1.8
FEATURE [Part::Box] Box053  label="pestania002"
  AttacherType = Attacher::AttachEngine3D
  Height = 7
  Length = 1
  Placement = pos=(100,19,-162.5) rot=(0,0,1;0rad)
  Width = 7
FEATURE [Part::Box] Box054  label="pestania003"
  AttacherType = Attacher::AttachEngine3D
  Height = 7
  Length = 1
  Placement = pos=(-89,19,-162.5) rot=(0,0,1;0rad)
  Width = 7
FEATURE [Part::Cylinder] Cylinder025
  Angle = 360
  AttacherType = Attacher::AttachEngine3D
  Height = 210
  Placement = pos=(-100,23,-158.5) rot=(0,1,0;1.5708rad)
  Radius = 1.8
FEATURE [Part::MultiFuse] Fusion007002009027003005008003003006005017002002002002002002002022
  Shapes = -> [Box053,Cut001001001002003001008002002033001001001001001001001002001001002001045002003017008007002010007002014003017041]
FEATURE [Part::Cut] Cut001001001002003001008002002033001001001001001001001002001001002001045002003017008007002010007002014003017045  label="placa_lateral_derecha_panal_2"
  Base = -> Fusion007002009027003005008003003006005017002002002002002002002022
  Tool = -> Cylinder025
FEATURE [Part::MultiFuse] Fusion007002009027003005008003003006005017002002002002002002002023
  Shapes = -> [Cut001001001002003001008002002033001001001001001001001002001001002001045002003017008007002010007002014003017042,Box054]
FEATURE [Part::Cut] Cut001001001002003001008002002033001001001001001001001002001001002001045002003017008007002010007002014003017046  label="placa_lateral_izquierda_panal_2"
  Base = -> Fusion007002009027003005008003003006005017002002002002002002002023
  Tool = -> Cylinder024
FEATURE [Part::Box] Box055  label="tapa001"
  AttacherType = Attacher::AttachEngine3D
  Height = 120
  Length = 188
  Placement = pos=(-88,19,-227) rot=(0,0,1;0rad)
  Width = 1
FEATURE [Part::Box] Box056  label="Cube034"
  AttacherType = Attacher::AttachEngine3D
  Height = 5
  Length = 10
  Placement = pos=(-91,14,-112) rot=(0,0,1;0rad)
  Width = 10
FEATURE [Part::Box] Box057  label="Cube035"
  AttacherType = Attacher::AttachEngine3D
  Height = 5
  Length = 10
  Placement = pos=(93,14,-112) rot=(0,0,1;0rad)
  Width = 10
FEATURE [Part::Box] Box058  label="Cube036"
  AttacherType = Attacher::AttachEngine3D
  Height = 5
  Length = 10
  Placement = pos=(93,14,-227.8) rot=(0,0,1;0rad)
  Width = 10
FEATURE [Part::Box] Box059  label="Cube037"
  AttacherType = Attacher::AttachEngine3D
  Height = 5
  Length = 10
  Placement = pos=(-91,14,-227.8) rot=(0,0,1;0rad)
  Width = 10
FEATURE [Part::Cut] Cut001001001002003001008002002033001001001001001001001002001001002001045002003017008007002010007002014003017047
  Base = -> Box055
  Tool = -> Box056
FEATURE [Part::Cut] Cut001001001002003001008002002033001001001001001001001002001001002001045002003017008007002010007002014003017048
  Base = -> Cut001001001002003001008002002033001001001001001001001002001001002001045002003017008007002010007002014003017047
  Tool = -> Box057
FEATURE [Part::Cut] Cut001001001002003001008002002033001001001001001001001002001001002001045002003017008007002010007002014003017049
  Base = -> Cut001001001002003001008002002033001001001001001001001002001001002001045002003017008007002010007002014003017048
  Tool = -> Box058
FEATURE [Part::Cut] Cut001001001002003001008002002033001001001001001001001002001001002001045002003017008007002010007002014003017050  label="placa_base_pura"
  Base = -> Cut001001001002003001008002002033001001001001001001001002001001002001045002003017008007002010007002014003017049
  Tool = -> Box059
FEATURE [Part::MultiFuse] Fusion007002009027003005008003003006005017002002002002002002002024
  Shapes = -> [Cut001001001002003001008002002033001001001001001001001002001001002001045002003017008007002010007002014003017050,Cut001001001002003001008002002033001001001001001001001002001001002001045002003017008007002010007002014003017044]
FEATURE [Part::MultiFuse] Fusion007002009027003005008003003006005017002002002002002002002025  label="placa_base_sin_panal"
  Shapes = -> [Fusion007002009027003005008003003006005017002002002002002002002024,Cut001001001002003001008002002033001001001001001001001002001001002001045002003017008007002010007002014003017043]
FEATURE [Part::Cylinder] Cylinder026
  Angle = 360
  AttacherType = Attacher::AttachEngine3D
  Height = 10
  Placement = pos=(-85,23,-229) rot=(0,0,1;0rad)
  Radius = 1.8
FEATURE [Part::Cylinder] Cylinder027
  Angle = 360
  AttacherType = Attacher::AttachEngine3D
  Height = 10
  Placement = pos=(97,23,-229) rot=(0,0,1;0rad)
  Radius = 1.8
FEATURE [Part::Cylinder] Cylinder028
  Angle = 360
  AttacherType = Attacher::AttachEngine3D
  Height = 10
  Placement = pos=(-85,85,-229) rot=(0,0,1;0rad)
  Radius = 1.8
FEATURE [Part::Cylinder] Cylinder029
  Angle = 360
  AttacherType = Attacher::AttachEngine3D
  Height = 10
  Placement = pos=(97,85,-229) rot=(0,0,1;0rad)
  Radius = 1.8
FEATURE [Part::Box] Box060  label="Cube038"
  AttacherType = Attacher::AttachEngine3D
  Height = 1
  Length = 190
  Placement = pos=(-89,19,-228) rot=(0,0,1;0rad)
  Width = 70
FEATURE [Part::Cut] Cut001001001002003001008002002033001001001001001001001002001001002001045002003017008007002010007002014003017051
  Base = -> Box060
  Tool = -> Cylinder026
FEATURE [Part::Cut] Cut001001001002003001008002002033001001001001001001001002001001002001045002003017008007002010007002014003017052
  Base = -> Cut001001001002003001008002002033001001001001001001001002001001002001045002003017008007002010007002014003017051
  Tool = -> Cylinder027
FEATURE [Part::Cut] Cut001001001002003001008002002033001001001001001001001002001001002001045002003017008007002010007002014003017053
  Base = -> Cut001001001002003001008002002033001001001001001001001002001001002001045002003017008007002010007002014003017052
  Tool = -> Cylinder028
FEATURE [Part::Cut] Cut001001001002003001008002002033001001001001001001001002001001002001045002003017008007002010007002014003017054  label="tapa_atras_sin_panal"
  Base = -> Cut001001001002003001008002002033001001001001001001001002001001002001045002003017008007002010007002014003017053
  Tool = -> Cylinder029
